# Revit family: 555002
name_source: partatom
category: Installations électriques
units: mm (PartAtom-declared; Revit-internal decimal feet)

## family parameters
Basée sur le plan de construction = Oui
Conserver l'orientation des annotations = Non
Cote de connecteur circulaire = Utiliser le diamètre
Couper avec des vides une fois chargée = Non
Numéro OmniClass = 23.75.35.17.17.11
Partagée = Non
Point de calcul de pièce = Non
Titre OmniClass = Ceiling Fans
Toujours verticalement = Non
Type d'élément = Normal

## types (1)
- 555002
    Charge apparente = 31 VA
    Couleur Corp = Valeur par défaut Nouveau Matériau
    Coût = 0 $
    Description = Brasseur d'air silencieux (<42db) équipé d'une platine LED.
Association de 3 pales d'un diamètre de 132cm permettant un débit de 10000m3/h.
Contient un moteur brushless avec 6 vitesses allant de 4W à 30W.
Brasseur d'air silencieux (<42db) équipé d'une platine LED
Couleur : Blanc
IP 20, IK 06
Diam. 1320mm
Flux restitué 1500lm
Conso. système 16.5W
Efficacité lumineuse produit complet 90.9lm/W
Diffuseur Polycarbonate Direct/Symétrique Opalescent, Corps en ABS
IRC 80
Garantie 5 ans
Empreinte carbone 1.03gCO2/h
Indice de réparabilité 6,3
    Elévation par défaut = 1219 mm
    Fabricant = Resistex
    IK = IK 06
    IP = IP 20
    Image du type = 555001_767x620.png
    Modèle = AUREA
    Tension = 230 V
    URL = https://www.resistex-sa.com
    Vitesse Max (tr/min) = 180 RPM
    indice de charge = Other
    nbr poles = 1

## geometry (parser evidence)
native form markers: Sweep x8
no freeform markers — native parametric forms only
